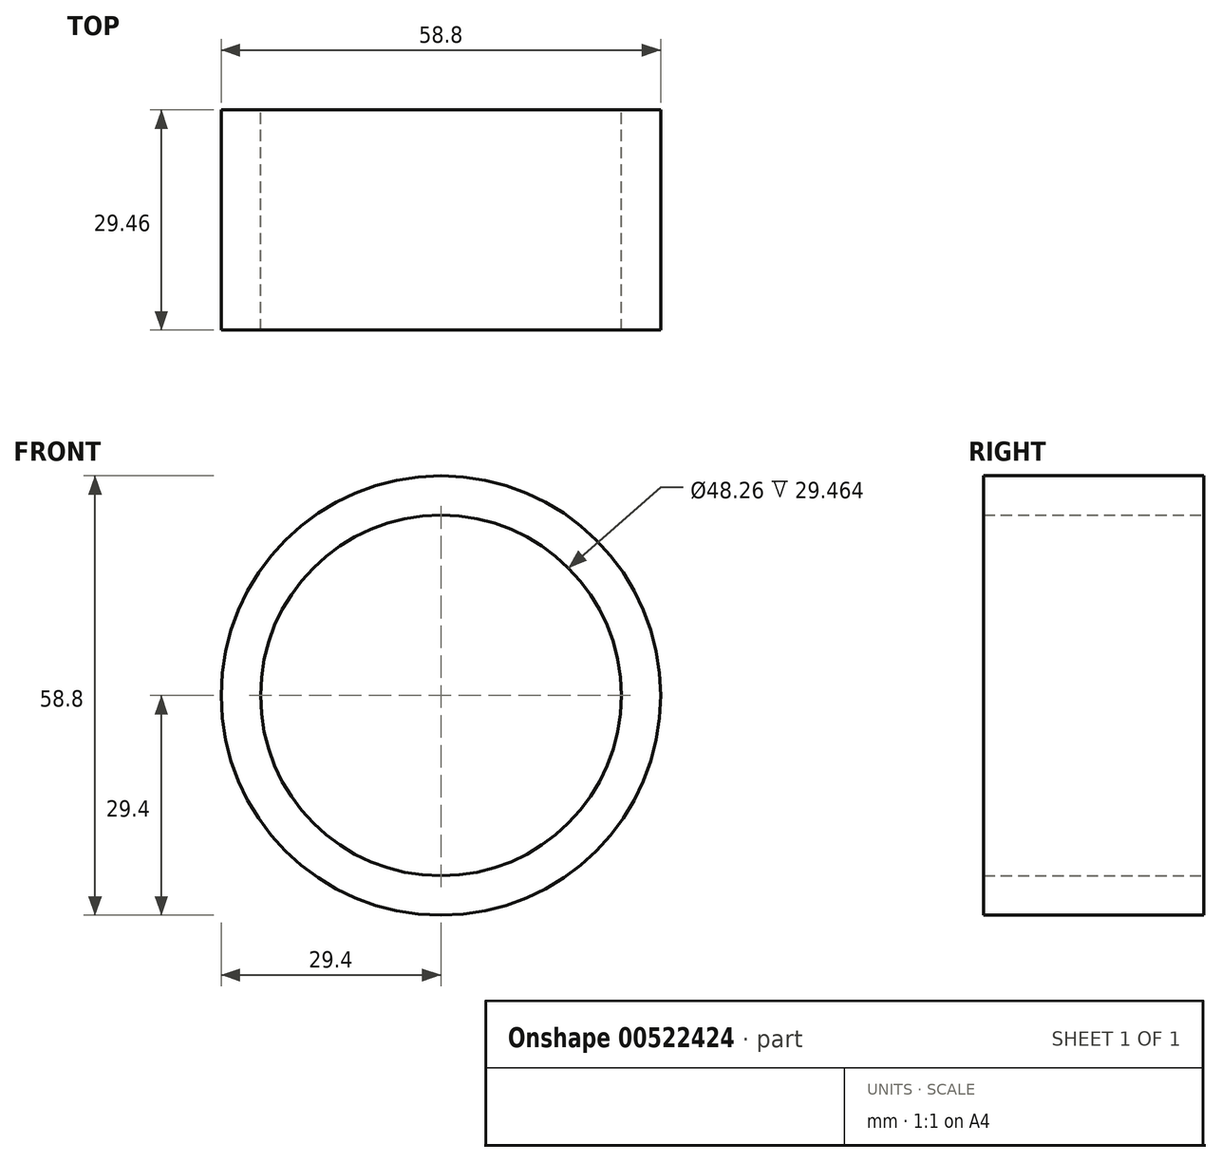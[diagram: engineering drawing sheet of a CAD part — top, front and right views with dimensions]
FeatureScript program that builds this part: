
annotation { "Feature Type Name" : "Feature", "Feature Type Description" : "" }
export const myFeature = defineFeature(function(context is Context, id is Id, definition is map)
    precondition{}
    {
        {
            var Q0;
            Q0=qCreatedBy(makeId("Front.planeOp"),FACE);
            var sketch = newSketch(context, id + "F0", { "sketchPlane" : qUnion([Q0])});
            skCircle(sketch, "E0", {"center": v(0, 0) * mm, "radius": 29.4 * mm});
            skCircle(sketch, "E1", {"center": v(0, 0) * mm, "radius": 24.13 * mm});
            skSolve(sketch);
        }
        {
            var Q0;
            Q0=makeQuery(id+"F0.imprint","IMPRINT",FACE,{"disambiguationData":[TD([[makeQuery(id+"F0.imprint","IMPRINT",EDGE,{"derivedFrom":sQuery(id+"F0.wireOp",EDGE,"E0")}),1.0]])]});
            extrude(context, id + "F1", {"entities" : qUnion([Q0]), "endBound" : BoundingType.SYMMETRIC, "depth" : 29.46 * mm, "offsetDistance" : 25.4 * mm});
        }
    });
